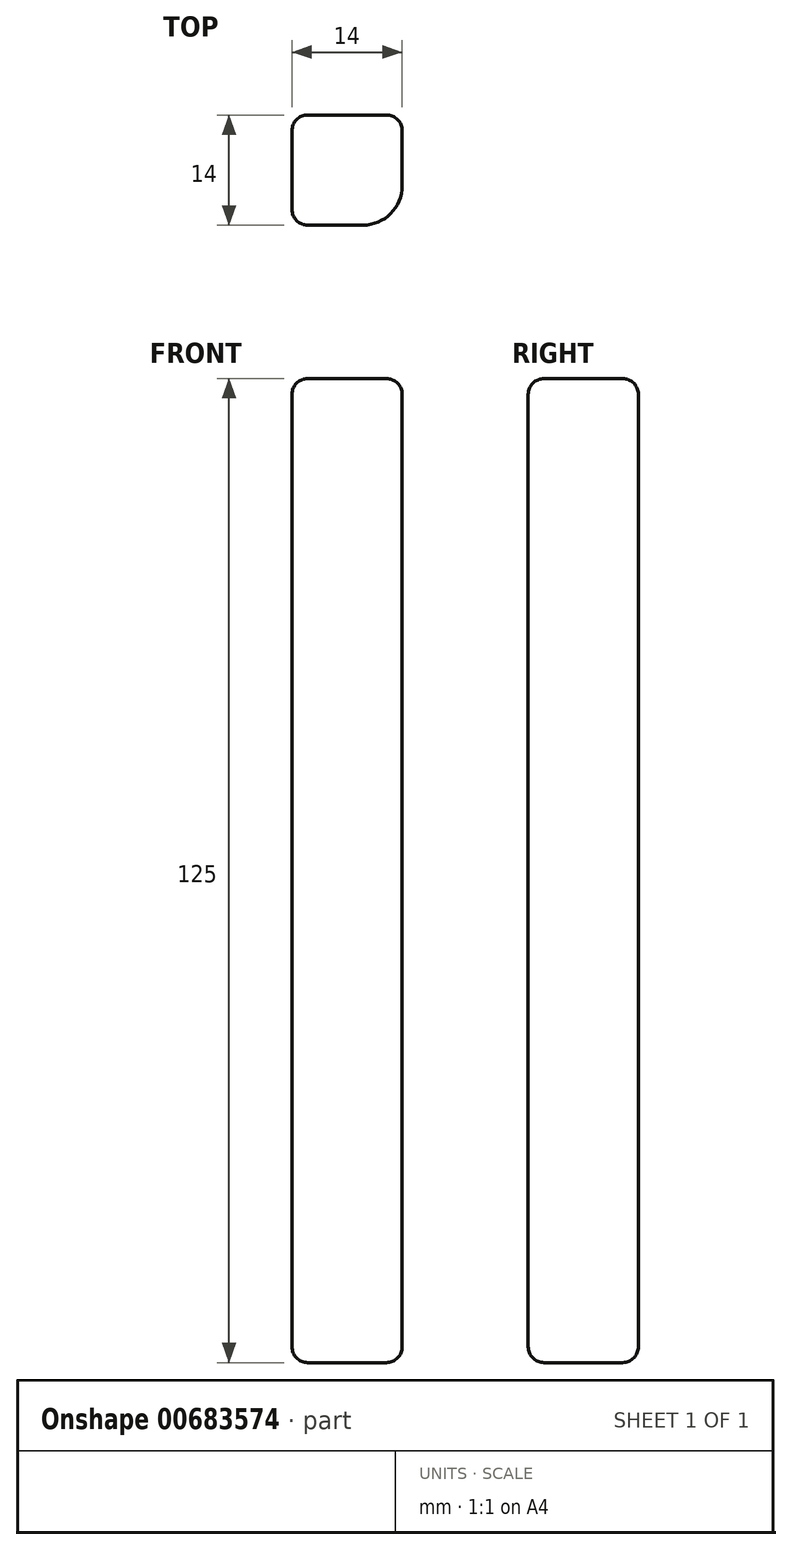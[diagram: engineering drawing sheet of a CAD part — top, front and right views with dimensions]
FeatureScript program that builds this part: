
annotation { "Feature Type Name" : "Feature", "Feature Type Description" : "" }
export const myFeature = defineFeature(function(context is Context, id is Id, definition is map)
    precondition{}
    {
        {
            var Q0;
            Q0=qCreatedBy(makeId("Top.planeOp"),FACE);
            var sketch = newSketch(context, id + "F0", { "sketchPlane" : qUnion([Q0])});
            skLineSegment(sketch, "E0", {"start": v(0, 0) * mm, "end": v(0, -14) * mm});
            skLineSegment(sketch, "E1", {"start": v(0, -14) * mm, "end": v(-14, -14) * mm});
            skLineSegment(sketch, "E2", {"start": v(-14, -14) * mm, "end": v(-14, 0) * mm});
            skLineSegment(sketch, "E3", {"start": v(-14, 0) * mm, "end": v(0, 0) * mm});
            skSolve(sketch);
        }
        {
            var Q0;
            Q0 = qSketchRegion(id + "F0", true);
            var Q1;
            Q1=makeQuery(id+"F0.imprint","IMPRINT",FACE,{"disambiguationData":[TD([[makeQuery(id+"F0.imprint","IMPRINT",EDGE,{"derivedFrom":sQuery(id+"F0.wireOp",EDGE,"E0")}),-1.0]])]});
            extrude(context, id + "F1", {"entities" : qUnion([Q0, Q1]), "depth" : 125 * mm, "offsetDistance" : 25 * mm});
        }
        {
            var Q0;
            Q0=makeQuery(id+"F1.opExtrude","CAP_EDGE",EDGE,{"disambiguationData":[OSD([sQuery(id+"F0.wireOp",EDGE,"E1")])],"isStart":false});
            var Q1;
            Q1=makeQuery(id+"F1.opExtrude","CAP_EDGE",EDGE,{"disambiguationData":[OSD([sQuery(id+"F0.wireOp",EDGE,"E0")])],"isStart":false});
            var Q2;
            Q2=makeQuery(id+"F1.opExtrude","CAP_EDGE",EDGE,{"disambiguationData":[OSD([sQuery(id+"F0.wireOp",EDGE,"E1")])],"isStart":true});
            var Q3;
            Q3=makeQuery(id+"F1.opExtrude","CAP_EDGE",EDGE,{"disambiguationData":[OSD([sQuery(id+"F0.wireOp",EDGE,"E0")])],"isStart":true});
            var Q4;
            Q4=makeQuery(id+"F1.opExtrude","CAP_EDGE",EDGE,{"disambiguationData":[OSD([sQuery(id+"F0.wireOp",EDGE,"E2")])],"isStart":false});
            var Q5;
            Q5=makeQuery(id+"F1.opExtrude","CAP_EDGE",EDGE,{"disambiguationData":[OSD([sQuery(id+"F0.wireOp",EDGE,"E3")])],"isStart":false});
            var Q6;
            Q6=makeQuery(id+"F1.opExtrude","SWEPT_FACE",FACE,{"disambiguationData":[OSD([sQuery(id+"F0.wireOp",EDGE,"E2")])]});
            fillet(context, id + "F2", {"entities" : qUnion([Q0, Q1, Q2, Q3, Q4, Q5, Q6]), "radius" : 2 * mm, "tangentPropagation" : true, "allowEdgeOverflow" : false});
        }
        {
            var Q0;
            Q0=makeQuery(id+"F1.opExtrude","SWEPT_EDGE",EDGE,{"disambiguationData":[OSD([sQuery(id+"F0.wireOp",EDGE,"E0"),sQuery(id+"F0.wireOp",EDGE,"E1")])]});
            fillet(context, id + "F3", {"entities" : qUnion([Q0]), "radius" : 5 * mm, "tangentPropagation" : true, "allowEdgeOverflow" : false});
        }
        {
            var Q0;
            Q0=makeQuery(id+"F1.opExtrude","SWEPT_EDGE",EDGE,{"disambiguationData":[OSD([sQuery(id+"F0.wireOp",EDGE,"E0"),sQuery(id+"F0.wireOp",EDGE,"E3")])]});
            var Q1;
            {var subQ0=sQuery(id+"F0.wireOp",EDGE,"E2");Q1=makeQuery(id+"F2.opFillet","BLEND_EDGE",EDGE,{"blendedFrom":[makeQuery(id+"F1.opExtrude","SWEPT_EDGE",EDGE,{"disambiguationData":[OSD([subQ0,sQuery(id+"F0.wireOp",EDGE,"E3")])]}),makeQuery(id+"F1.opExtrude","SWEPT_FACE",FACE,{"disambiguationData":[OSD([subQ0])]})],"blendedInto":[makeQuery(id+"F1.opExtrude","SWEPT_FACE",FACE,{"disambiguationData":[OSD([subQ0])]})]});}
            fillet(context, id + "F4", {"entities" : qUnion([Q0, Q1]), "radius" : 2 * mm, "tangentPropagation" : true, "allowEdgeOverflow" : false});
        }
    });
